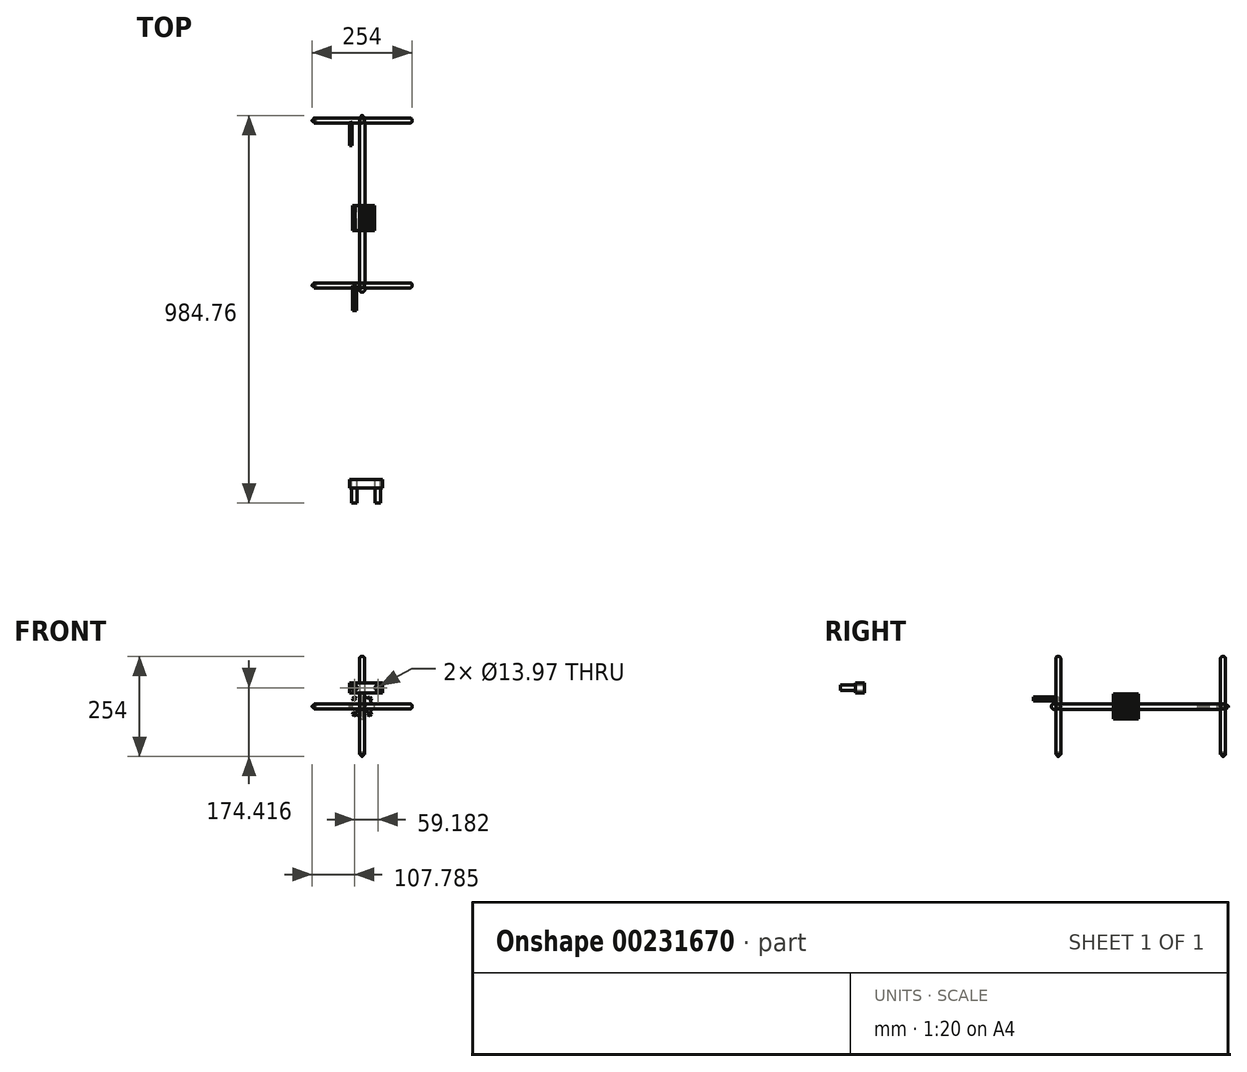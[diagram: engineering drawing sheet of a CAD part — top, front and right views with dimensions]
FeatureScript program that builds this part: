
annotation { "Feature Type Name" : "Feature", "Feature Type Description" : "" }
export const myFeature = defineFeature(function(context is Context, id is Id, definition is map)
    precondition{}
    {
        {
            var Q0;
            Q0=qCreatedBy(makeId("Front.planeOp"),FACE);
            var sketch = newSketch(context, id + "F0", { "sketchPlane" : qUnion([Q0])});
            skLineSegment(sketch, "E0", {"start": v(0, 0) * mm, "end": v(-17.96, 17.96) * mm});
            skArc(sketch, "E1", {"start": v(-17.96, 17.96) * mm, "mid": v(-9.72, 23.47) * mm, "end": v(0, 25.4) * mm});
            skLineSegment(sketch, "E2", {"start": v(0, 25.4) * mm, "end": v(0, 0) * mm});
            skLineSegment(sketch, "E3", {"start": v(-17.96, 17.96) * mm, "end": v(-22.45, 22.45) * mm});
            skLineSegment(sketch, "E4", {"start": v(-22.45, 22.45) * mm, "end": v(-20.65, 24.25) * mm});
            skLineSegment(sketch, "E5", {"start": v(-20.65, 24.25) * mm, "end": v(-14.3, 20.99) * mm});
            skLineSegment(sketch, "E6", {"start": v(0, 25.4) * mm, "end": v(0, 31.75) * mm});
            skLineSegment(sketch, "E7", {"start": v(0, 31.75) * mm, "end": v(-2.54, 31.75) * mm});
            skLineSegment(sketch, "E8", {"start": v(-2.54, 31.75) * mm, "end": v(-4.68, 24.97) * mm});
            skLineSegment(sketch, "E9.MirrorCS", {"start": v(0, 31.75) * mm, "end": v(2.54, 31.75) * mm});
            skLineSegment(sketch, "E10.MirrorCS", {"start": v(2.54, 31.75) * mm, "end": v(4.68, 24.97) * mm});
            skArc(sketch, "E11.MirrorCS", {"start": v(17.96, 17.96) * mm, "mid": v(9.72, 23.47) * mm, "end": v(0, 25.4) * mm});
            skLineSegment(sketch, "E12.MirrorCS", {"start": v(0, 0) * mm, "end": v(17.96, 17.96) * mm});
            skLineSegment(sketch, "E13.MirrorCS", {"start": v(20.65, 24.25) * mm, "end": v(14.3, 20.99) * mm});
            skLineSegment(sketch, "E14.MirrorCS", {"start": v(17.96, 17.96) * mm, "end": v(22.45, 22.45) * mm});
            skLineSegment(sketch, "E15.MirrorCS", {"start": v(22.45, 22.45) * mm, "end": v(20.65, 24.25) * mm});
            skLineSegment(sketch, "E16.MirrorCS", {"start": v(-22.45, -22.45) * mm, "end": v(-20.65, -24.25) * mm});
            skLineSegment(sketch, "E17.MirrorCS", {"start": v(0, -31.75) * mm, "end": v(2.54, -31.75) * mm});
            skLineSegment(sketch, "E18.MirrorCS", {"start": v(0, -31.75) * mm, "end": v(-2.54, -31.75) * mm});
            skLineSegment(sketch, "E19.MirrorCS", {"start": v(22.45, -22.45) * mm, "end": v(20.65, -24.25) * mm});
            skLineSegment(sketch, "E20.MirrorCS", {"start": v(-2.54, -31.75) * mm, "end": v(-4.68, -24.97) * mm});
            skLineSegment(sketch, "E21.MirrorCS", {"start": v(-20.65, -24.25) * mm, "end": v(-14.3, -20.99) * mm});
            skLineSegment(sketch, "E22.MirrorCS", {"start": v(-17.96, -17.96) * mm, "end": v(-22.45, -22.45) * mm});
            skLineSegment(sketch, "E23.MirrorCS", {"start": v(2.54, -31.75) * mm, "end": v(4.68, -24.97) * mm});
            skLineSegment(sketch, "E24.MirrorCS", {"start": v(20.65, -24.25) * mm, "end": v(14.3, -20.99) * mm});
            skArc(sketch, "E25.MirrorCS", {"start": v(17.96, -17.96) * mm, "mid": v(9.72, -23.47) * mm, "end": v(0, -25.4) * mm});
            skArc(sketch, "E26.MirrorCS", {"start": v(-17.96, -17.96) * mm, "mid": v(-9.72, -23.47) * mm, "end": v(0, -25.4) * mm});
            skLineSegment(sketch, "E27.MirrorCS", {"start": v(0, -25.4) * mm, "end": v(0, -31.75) * mm});
            skLineSegment(sketch, "E28.MirrorCS", {"start": v(17.96, -17.96) * mm, "end": v(22.45, -22.45) * mm});
            skLineSegment(sketch, "E29.MirrorCS", {"start": v(0, -25.4) * mm, "end": v(0, 0) * mm});
            skLineSegment(sketch, "E30.MirrorCS", {"start": v(0, 0) * mm, "end": v(17.96, -17.96) * mm});
            skLineSegment(sketch, "E31.MirrorCS", {"start": v(0, 0) * mm, "end": v(-17.96, -17.96) * mm});
            skLineSegment(sketch, "E32", {"start": v(-17.96, -17.96) * mm, "end": v(-29.23, -29.23) * mm, "construction": true});
            skLineSegment(sketch, "E33", {"start": v(-29.23, -29.23) * mm, "end": v(22.45, 22.45) * mm, "construction": true});
            skLineSegment(sketch, "E34.MirrorCS", {"start": v(24.25, -20.65) * mm, "end": v(20.99, -14.3) * mm});
            skLineSegment(sketch, "E35.MirrorCS", {"start": v(22.45, -22.45) * mm, "end": v(24.25, -20.65) * mm});
            skArc(sketch, "E36.MirrorCS", {"start": v(17.96, -17.96) * mm, "mid": v(23.47, -9.72) * mm, "end": v(25.4, 0) * mm});
            skArc(sketch, "E37.MirrorCS", {"start": v(17.96, 17.96) * mm, "mid": v(23.47, 9.72) * mm, "end": v(25.4, 0) * mm});
            skLineSegment(sketch, "E38.MirrorCS", {"start": v(24.25, 20.65) * mm, "end": v(20.99, 14.3) * mm});
            skLineSegment(sketch, "E39.MirrorCS", {"start": v(22.45, 22.45) * mm, "end": v(24.25, 20.65) * mm});
            skLineSegment(sketch, "E40.MirrorCS", {"start": v(25.4, 0) * mm, "end": v(31.75, 0) * mm});
            skLineSegment(sketch, "E41.MirrorCS", {"start": v(31.75, 0) * mm, "end": v(31.75, 2.54) * mm});
            skLineSegment(sketch, "E42.MirrorCS", {"start": v(31.75, 2.54) * mm, "end": v(24.97, 4.68) * mm});
            skLineSegment(sketch, "E43.MirrorCS", {"start": v(31.75, -2.54) * mm, "end": v(24.97, -4.68) * mm});
            skLineSegment(sketch, "E44.MirrorCS", {"start": v(31.75, 0) * mm, "end": v(31.75, -2.54) * mm});
            skLineSegment(sketch, "E45.MirrorCS", {"start": v(-24.25, -20.65) * mm, "end": v(-20.99, -14.3) * mm});
            skLineSegment(sketch, "E46.MirrorCS", {"start": v(-22.45, -22.45) * mm, "end": v(-24.25, -20.65) * mm});
            skArc(sketch, "E47.MirrorCS", {"start": v(-17.96, -17.96) * mm, "mid": v(-23.47, -9.72) * mm, "end": v(-25.4, 0) * mm});
            skArc(sketch, "E48.MirrorCS", {"start": v(-17.96, 17.96) * mm, "mid": v(-23.47, 9.72) * mm, "end": v(-25.4, 0) * mm});
            skLineSegment(sketch, "E49.MirrorCS", {"start": v(-31.75, 2.54) * mm, "end": v(-24.97, 4.68) * mm});
            skLineSegment(sketch, "E50.MirrorCS", {"start": v(-31.75, -2.54) * mm, "end": v(-24.97, -4.68) * mm});
            skLineSegment(sketch, "E51.MirrorCS", {"start": v(-24.25, 20.65) * mm, "end": v(-20.99, 14.3) * mm});
            skLineSegment(sketch, "E52.MirrorCS", {"start": v(-22.45, 22.45) * mm, "end": v(-24.25, 20.65) * mm});
            skLineSegment(sketch, "E53.MirrorCS", {"start": v(-31.75, 0) * mm, "end": v(-31.75, 2.54) * mm});
            skLineSegment(sketch, "E54.MirrorCS", {"start": v(-31.75, 0) * mm, "end": v(-31.75, -2.54) * mm});
            skCircle(sketch, "E55", {"center": v(0, 0) * mm, "radius": 6.99 * mm});
            skSolve(sketch);
        }
        {
            var Q0;
            {var subQ0=sQuery(id+"F0.wireOp",EDGE,"E6");Q0=makeQuery(id+"F0.imprint","IMPRINT",FACE,{"disambiguationData":[TD([[makeQuery(id+"F0.imprint","IMPRINT",EDGE,{"derivedFrom":subQ0}),-1.0]])]});}
            var Q1;
            {var subQ0=sQuery(id+"F0.wireOp",EDGE,"E6");Q1=makeQuery(id+"F0.imprint","IMPRINT",FACE,{"disambiguationData":[TD([[makeQuery(id+"F0.imprint","IMPRINT",EDGE,{"derivedFrom":subQ0}),1.0]])]});}
            var Q2;
            {var subQ1=sQuery(id+"F0.wireOp",EDGE,"E1");var subQ4=makeQuery(id+"F0.imprint","INTERSECT",VERTEX,{"derivedFrom":[subQ1,sQuery(id+"F0.wireOp",EDGE,"E5")]});Q2=makeQuery(id+"F0.imprint","IMPRINT",FACE,{"disambiguationData":[TD([[makeQuery(id+"F0.imprint","IMPRINT",EDGE,{"disambiguationData":[TD([[subQ4,-1.0]])],"derivedFrom":subQ1}),-1.0]])]});}
            var Q3;
            {var subQ0=sQuery(id+"F0.wireOp",EDGE,"E3");Q3=makeQuery(id+"F0.imprint","IMPRINT",FACE,{"disambiguationData":[TD([[makeQuery(id+"F0.imprint","IMPRINT",EDGE,{"derivedFrom":subQ0}),-1.0]])]});}
            var Q4;
            {var subQ0=sQuery(id+"F0.wireOp",EDGE,"E3");Q4=makeQuery(id+"F0.imprint","IMPRINT",FACE,{"disambiguationData":[TD([[makeQuery(id+"F0.imprint","IMPRINT",EDGE,{"derivedFrom":subQ0}),1.0]])]});}
            var Q5;
            {var subQ0=sQuery(id+"F0.wireOp",EDGE,"E47.MirrorCS");var subQ1=makeQuery(id+"F0.imprint","INTERSECT",VERTEX,{"derivedFrom":[sQuery(id+"F0.wireOp",EDGE,"E45.MirrorCS"),subQ0]});Q5=makeQuery(id+"F0.imprint","IMPRINT",FACE,{"disambiguationData":[TD([[makeQuery(id+"F0.imprint","IMPRINT",EDGE,{"disambiguationData":[TD([[subQ1,-1.0]])],"derivedFrom":subQ0}),-1.0]])]});}
            var Q6;
            {var subQ1=sQuery(id+"F0.wireOp",EDGE,"E26.MirrorCS");var subQ5=makeQuery(id+"F0.imprint","INTERSECT",VERTEX,{"derivedFrom":[sQuery(id+"F0.wireOp",EDGE,"E20.MirrorCS"),subQ1]});Q6=makeQuery(id+"F0.imprint","IMPRINT",FACE,{"disambiguationData":[TD([[makeQuery(id+"F0.imprint","IMPRINT",EDGE,{"disambiguationData":[TD([[subQ5,1.0]])],"derivedFrom":subQ1}),1.0]])]});}
            var Q7;
            {var subQ0=sQuery(id+"F0.wireOp",EDGE,"E25.MirrorCS");var subQ1=makeQuery(id+"F0.imprint","INTERSECT",VERTEX,{"derivedFrom":[sQuery(id+"F0.wireOp",EDGE,"E23.MirrorCS"),subQ0]});Q7=makeQuery(id+"F0.imprint","IMPRINT",FACE,{"disambiguationData":[TD([[makeQuery(id+"F0.imprint","IMPRINT",EDGE,{"disambiguationData":[TD([[subQ1,1.0]])],"derivedFrom":subQ0}),-1.0]])]});}
            var Q8;
            {var subQ0=sQuery(id+"F0.wireOp",EDGE,"E36.MirrorCS");var subQ3=makeQuery(id+"F0.imprint","INTERSECT",VERTEX,{"derivedFrom":[sQuery(id+"F0.wireOp",EDGE,"E34.MirrorCS"),subQ0]});Q8=makeQuery(id+"F0.imprint","IMPRINT",FACE,{"disambiguationData":[TD([[makeQuery(id+"F0.imprint","IMPRINT",EDGE,{"disambiguationData":[TD([[subQ3,-1.0]])],"derivedFrom":subQ0}),1.0]])]});}
            var Q9;
            {var subQ0=sQuery(id+"F0.wireOp",EDGE,"E11.MirrorCS");var subQ3=makeQuery(id+"F0.imprint","INTERSECT",VERTEX,{"derivedFrom":[sQuery(id+"F0.wireOp",EDGE,"E10.MirrorCS"),subQ0]});Q9=makeQuery(id+"F0.imprint","IMPRINT",FACE,{"disambiguationData":[TD([[makeQuery(id+"F0.imprint","IMPRINT",EDGE,{"disambiguationData":[TD([[subQ3,1.0]])],"derivedFrom":subQ0}),1.0]])]});}
            var Q10;
            {var subQ0=sQuery(id+"F0.wireOp",EDGE,"E14.MirrorCS");Q10=makeQuery(id+"F0.imprint","IMPRINT",FACE,{"disambiguationData":[TD([[makeQuery(id+"F0.imprint","IMPRINT",EDGE,{"derivedFrom":subQ0}),-1.0]])]});}
            var Q11;
            {var subQ2=sQuery(id+"F0.wireOp",EDGE,"E13.MirrorCS");Q11=makeQuery(id+"F0.imprint","IMPRINT",FACE,{"disambiguationData":[TD([[makeQuery(id+"F0.imprint","IMPRINT",EDGE,{"derivedFrom":subQ2}),1.0]])]});}
            var Q12;
            {var subQ0=sQuery(id+"F0.wireOp",EDGE,"E40.MirrorCS");Q12=makeQuery(id+"F0.imprint","IMPRINT",FACE,{"disambiguationData":[TD([[makeQuery(id+"F0.imprint","IMPRINT",EDGE,{"derivedFrom":subQ0}),1.0]])]});}
            var Q13;
            {var subQ0=sQuery(id+"F0.wireOp",EDGE,"E40.MirrorCS");Q13=makeQuery(id+"F0.imprint","IMPRINT",FACE,{"disambiguationData":[TD([[makeQuery(id+"F0.imprint","IMPRINT",EDGE,{"derivedFrom":subQ0}),-1.0]])]});}
            var Q14;
            {var subQ0=sQuery(id+"F0.wireOp",EDGE,"E34.MirrorCS");Q14=makeQuery(id+"F0.imprint","IMPRINT",FACE,{"disambiguationData":[TD([[makeQuery(id+"F0.imprint","IMPRINT",EDGE,{"derivedFrom":subQ0}),1.0]])]});}
            var Q15;
            Q15=makeQuery(id+"F0.imprint","IMPRINT",FACE,{"disambiguationData":[TD([[makeQuery(id+"F0.imprint","IMPRINT",EDGE,{"derivedFrom":sQuery(id+"F0.wireOp",EDGE,"E19.MirrorCS")}),-1.0]])]});
            var Q16;
            Q16=makeQuery(id+"F0.imprint","IMPRINT",FACE,{"disambiguationData":[TD([[makeQuery(id+"F0.imprint","IMPRINT",EDGE,{"derivedFrom":sQuery(id+"F0.wireOp",EDGE,"E17.MirrorCS")}),1.0]])]});
            var Q17;
            Q17=makeQuery(id+"F0.imprint","IMPRINT",FACE,{"disambiguationData":[TD([[makeQuery(id+"F0.imprint","IMPRINT",EDGE,{"derivedFrom":sQuery(id+"F0.wireOp",EDGE,"E18.MirrorCS")}),-1.0]])]});
            var Q18;
            Q18=makeQuery(id+"F0.imprint","IMPRINT",FACE,{"disambiguationData":[TD([[makeQuery(id+"F0.imprint","IMPRINT",EDGE,{"derivedFrom":sQuery(id+"F0.wireOp",EDGE,"E16.MirrorCS")}),1.0]])]});
            var Q19;
            {var subQ0=sQuery(id+"F0.wireOp",EDGE,"E22.MirrorCS");Q19=makeQuery(id+"F0.imprint","IMPRINT",FACE,{"disambiguationData":[TD([[makeQuery(id+"F0.imprint","IMPRINT",EDGE,{"derivedFrom":subQ0}),-1.0]])]});}
            var Q20;
            {var subQ1=sQuery(id+"F0.wireOp",EDGE,"E49.MirrorCS");Q20=makeQuery(id+"F0.imprint","IMPRINT",FACE,{"disambiguationData":[TD([[makeQuery(id+"F0.imprint","IMPRINT",EDGE,{"derivedFrom":subQ1}),-1.0]])]});}
            extrude(context, id + "F1", {"entities" : qUnion([Q0, Q1, Q2, Q3, Q4, Q5, Q6, Q7, Q8, Q9, Q10, Q11, Q12, Q13, Q14, Q15, Q16, Q17, Q18, Q19, Q20]), "depth" : 63.5 * mm});
        }
        {
            var Q0;
            Q0=qCreatedBy(makeId("Front.planeOp"),FACE);
            var sketch = newSketch(context, id + "F2", { "sketchPlane" : qUnion([Q0])});
            skLineSegment(sketch, "E56", {"start": v(-19.22, 47.42) * mm, "end": v(39.97, 47.42) * mm, "construction": true});
            skCircle(sketch, "E57", {"center": v(-19.22, 47.42) * mm, "radius": 6.99 * mm});
            skCircle(sketch, "E58", {"center": v(39.97, 47.42) * mm, "radius": 6.99 * mm});
            skLineSegment(sketch, "E59.bottom", {"start": v(52.67, 60.12) * mm, "end": v(-31.92, 60.12) * mm});
            skLineSegment(sketch, "E59.top", {"start": v(52.67, 34.72) * mm, "end": v(-31.92, 34.72) * mm});
            skLineSegment(sketch, "E59.left", {"start": v(52.67, 60.12) * mm, "end": v(52.67, 34.72) * mm});
            skLineSegment(sketch, "E59.right", {"start": v(-31.92, 60.12) * mm, "end": v(-31.92, 34.72) * mm});
            skPoint(sketch, "E59.middle", {"position": v(10.38, 47.42) * mm});
            skSolve(sketch);
        }
        {
            var Q0;
            Q0=makeQuery(id+"F2.imprint","IMPRINT",FACE,{"disambiguationData":[TD([[makeQuery(id+"F2.imprint","IMPRINT",EDGE,{"derivedFrom":sQuery(id+"F2.wireOp",EDGE,"E57")}),1.0]])]});
            var Q1;
            Q1=makeQuery(id+"F2.imprint","IMPRINT",FACE,{"disambiguationData":[TD([[makeQuery(id+"F2.imprint","IMPRINT",EDGE,{"derivedFrom":sQuery(id+"F2.wireOp",EDGE,"E58")}),1.0]])]});
            extrude(context, id + "F3", {"entities" : qUnion([Q0, Q1]), "depth" : 60.2 * mm});
        }
        {
            var Q0;
            Q0 = qSketchRegion(id + "F2", true);
            extrude(context, id + "F4", {"entities" : qUnion([Q0]), "depth" : 22.35 * mm});
        }
        {
            var Q0;
            {var subQ1=sQuery(id+"F0.wireOp",EDGE,"E29.MirrorCS");var subQ3=sQuery(id+"F0.wireOp",EDGE,"E55");var subQ4=makeQuery(id+"F0.imprint","INTERSECT",VERTEX,{"derivedFrom":[subQ1,subQ3]});Q0=makeQuery(id+"F0.imprint","IMPRINT",FACE,{"disambiguationData":[TD([[makeQuery(id+"F0.imprint","IMPRINT",EDGE,{"disambiguationData":[TD([[subQ4,-1.0]])],"derivedFrom":subQ3}),1.0]])]});}
            var Q1;
            {var subQ1=sQuery(id+"F0.wireOp",EDGE,"E29.MirrorCS");var subQ3=sQuery(id+"F0.wireOp",EDGE,"E55");var subQ4=makeQuery(id+"F0.imprint","INTERSECT",VERTEX,{"derivedFrom":[subQ1,subQ3]});Q1=makeQuery(id+"F0.imprint","IMPRINT",FACE,{"disambiguationData":[TD([[makeQuery(id+"F0.imprint","IMPRINT",EDGE,{"disambiguationData":[TD([[subQ4,1.0]])],"derivedFrom":subQ3}),1.0]])]});}
            var Q2;
            {var subQ1=sQuery(id+"F0.wireOp",EDGE,"E0");var subQ3=sQuery(id+"F0.wireOp",EDGE,"E55");var subQ4=makeQuery(id+"F0.imprint","INTERSECT",VERTEX,{"derivedFrom":[subQ1,subQ3]});Q2=makeQuery(id+"F0.imprint","IMPRINT",FACE,{"disambiguationData":[TD([[makeQuery(id+"F0.imprint","IMPRINT",EDGE,{"disambiguationData":[TD([[subQ4,-1.0]])],"derivedFrom":subQ3}),1.0]])]});}
            var Q3;
            {var subQ1=sQuery(id+"F0.wireOp",EDGE,"E0");var subQ3=sQuery(id+"F0.wireOp",EDGE,"E55");var subQ4=makeQuery(id+"F0.imprint","INTERSECT",VERTEX,{"derivedFrom":[subQ1,subQ3]});Q3=makeQuery(id+"F0.imprint","IMPRINT",FACE,{"disambiguationData":[TD([[makeQuery(id+"F0.imprint","IMPRINT",EDGE,{"disambiguationData":[TD([[subQ4,1.0]])],"derivedFrom":subQ3}),1.0]])]});}
            var Q4;
            {var subQ1=sQuery(id+"F0.wireOp",EDGE,"E2");var subQ3=sQuery(id+"F0.wireOp",EDGE,"E55");var subQ4=makeQuery(id+"F0.imprint","INTERSECT",VERTEX,{"derivedFrom":[subQ1,subQ3]});Q4=makeQuery(id+"F0.imprint","IMPRINT",FACE,{"disambiguationData":[TD([[makeQuery(id+"F0.imprint","IMPRINT",EDGE,{"disambiguationData":[TD([[subQ4,1.0]])],"derivedFrom":subQ3}),1.0]])]});}
            var Q5;
            {var subQ1=sQuery(id+"F0.wireOp",EDGE,"E12.MirrorCS");var subQ3=sQuery(id+"F0.wireOp",EDGE,"E55");var subQ4=makeQuery(id+"F0.imprint","INTERSECT",VERTEX,{"derivedFrom":[subQ1,subQ3]});Q5=makeQuery(id+"F0.imprint","IMPRINT",FACE,{"disambiguationData":[TD([[makeQuery(id+"F0.imprint","IMPRINT",EDGE,{"disambiguationData":[TD([[subQ4,1.0]])],"derivedFrom":subQ3}),1.0]])]});}
            extrude(context, id + "F5", {"entities" : qUnion([Q0, Q1, Q2, Q3, Q4, Q5]), "operationType" : NewBodyOperationType.ADD, "oppositeDirection" : true, "depth" : 228.6 * mm, "hasSecondDirection" : true, "secondDirectionOppositeDirection" : false, "secondDirectionDepth" : 219.96 * mm});
        }
        {
            var Q0;
            Q0=makeQuery(id+"F1.opExtrude","SWEPT_BODY",BODY,{"disambiguationData":[OSD([sQuery(id+"F0.wireOp",EDGE,"E1"),sQuery(id+"F0.wireOp",EDGE,"E4"),sQuery(id+"F0.wireOp",EDGE,"E5"),sQuery(id+"F0.wireOp",EDGE,"E7"),sQuery(id+"F0.wireOp",EDGE,"E8"),sQuery(id+"F0.wireOp",EDGE,"E9.MirrorCS"),sQuery(id+"F0.wireOp",EDGE,"E10.MirrorCS"),sQuery(id+"F0.wireOp",EDGE,"E11.MirrorCS"),sQuery(id+"F0.wireOp",EDGE,"E13.MirrorCS"),sQuery(id+"F0.wireOp",EDGE,"E15.MirrorCS"),sQuery(id+"F0.wireOp",EDGE,"E16.MirrorCS"),sQuery(id+"F0.wireOp",EDGE,"E17.MirrorCS"),sQuery(id+"F0.wireOp",EDGE,"E18.MirrorCS"),sQuery(id+"F0.wireOp",EDGE,"E19.MirrorCS"),sQuery(id+"F0.wireOp",EDGE,"E20.MirrorCS"),sQuery(id+"F0.wireOp",EDGE,"E21.MirrorCS"),sQuery(id+"F0.wireOp",EDGE,"E23.MirrorCS"),sQuery(id+"F0.wireOp",EDGE,"E24.MirrorCS"),sQuery(id+"F0.wireOp",EDGE,"E25.MirrorCS"),sQuery(id+"F0.wireOp",EDGE,"E26.MirrorCS"),sQuery(id+"F0.wireOp",EDGE,"E34.MirrorCS"),sQuery(id+"F0.wireOp",EDGE,"E35.MirrorCS"),sQuery(id+"F0.wireOp",EDGE,"E36.MirrorCS"),sQuery(id+"F0.wireOp",EDGE,"E37.MirrorCS"),sQuery(id+"F0.wireOp",EDGE,"E38.MirrorCS"),sQuery(id+"F0.wireOp",EDGE,"E39.MirrorCS"),sQuery(id+"F0.wireOp",EDGE,"E41.MirrorCS"),sQuery(id+"F0.wireOp",EDGE,"E42.MirrorCS"),sQuery(id+"F0.wireOp",EDGE,"E43.MirrorCS"),sQuery(id+"F0.wireOp",EDGE,"E44.MirrorCS"),sQuery(id+"F0.wireOp",EDGE,"E45.MirrorCS"),sQuery(id+"F0.wireOp",EDGE,"E46.MirrorCS"),sQuery(id+"F0.wireOp",EDGE,"E47.MirrorCS"),sQuery(id+"F0.wireOp",EDGE,"E48.MirrorCS"),sQuery(id+"F0.wireOp",EDGE,"E49.MirrorCS"),sQuery(id+"F0.wireOp",EDGE,"E50.MirrorCS"),sQuery(id+"F0.wireOp",EDGE,"E51.MirrorCS"),sQuery(id+"F0.wireOp",EDGE,"E52.MirrorCS"),sQuery(id+"F0.wireOp",EDGE,"E53.MirrorCS"),sQuery(id+"F0.wireOp",EDGE,"E54.MirrorCS"),sQuery(id+"F0.wireOp",EDGE,"E55")])]});
            transform(context, id + "F6", {"entities" : qUnion([Q0]), "transformType" : TransformType.TRANSLATION_3D, "dx" : 0 * mm, "dy" : -132.08 * mm, "dz" : 0 * mm, "makeCopy" : false});
        }
        {
            var Q0;
            Q0=makeQuery(id+"F5.opExtrude","CAP_EDGE",EDGE,{"disambiguationData":[OSD([sQuery(id+"F0.wireOp",EDGE,"E55")])],"isStart":false});
            var Q1;
            Q1=makeQuery(id+"FoJtG7K4DBaO0Y3_4.opExtrude","CAP_EDGE",EDGE,{"disambiguationData":[OSD([sQuery(id+"FWvqbfKtp3cxLVg_4.wireOp",EDGE,"aRqvi6iJ-hhy7-xzrE-r3em-tmQ5B9AIq148")])],"isStart":true});
            var Q2;
            Q2=makeQuery(id+"FoJtG7K4DBaO0Y3_4.opExtrude","CAP_EDGE",EDGE,{"disambiguationData":[OSD([sQuery(id+"FWvqbfKtp3cxLVg_4.wireOp",EDGE,"aRqvi6iJ-hhy7-xzrE-r3em-tmQ5B9AIq148")])],"isStart":false});
            fillet(context, id + "F7", {"entities" : qUnion([Q0, Q1, Q2]), "radius" : 5.08 * mm, "tangentPropagation" : true, "allowEdgeOverflow" : false});
        }
        {
            var Q0;
            Q0=makeQuery(id+"F1.opExtrude","SWEPT_BODY",BODY,{"disambiguationData":[OSD([sQuery(id+"F0.wireOp",EDGE,"E1"),sQuery(id+"F0.wireOp",EDGE,"E4"),sQuery(id+"F0.wireOp",EDGE,"E5"),sQuery(id+"F0.wireOp",EDGE,"E7"),sQuery(id+"F0.wireOp",EDGE,"E8"),sQuery(id+"F0.wireOp",EDGE,"E9.MirrorCS"),sQuery(id+"F0.wireOp",EDGE,"E10.MirrorCS"),sQuery(id+"F0.wireOp",EDGE,"E11.MirrorCS"),sQuery(id+"F0.wireOp",EDGE,"E13.MirrorCS"),sQuery(id+"F0.wireOp",EDGE,"E15.MirrorCS"),sQuery(id+"F0.wireOp",EDGE,"E16.MirrorCS"),sQuery(id+"F0.wireOp",EDGE,"E17.MirrorCS"),sQuery(id+"F0.wireOp",EDGE,"E18.MirrorCS"),sQuery(id+"F0.wireOp",EDGE,"E19.MirrorCS"),sQuery(id+"F0.wireOp",EDGE,"E20.MirrorCS"),sQuery(id+"F0.wireOp",EDGE,"E21.MirrorCS"),sQuery(id+"F0.wireOp",EDGE,"E23.MirrorCS"),sQuery(id+"F0.wireOp",EDGE,"E24.MirrorCS"),sQuery(id+"F0.wireOp",EDGE,"E25.MirrorCS"),sQuery(id+"F0.wireOp",EDGE,"E26.MirrorCS"),sQuery(id+"F0.wireOp",EDGE,"E34.MirrorCS"),sQuery(id+"F0.wireOp",EDGE,"E35.MirrorCS"),sQuery(id+"F0.wireOp",EDGE,"E36.MirrorCS"),sQuery(id+"F0.wireOp",EDGE,"E37.MirrorCS"),sQuery(id+"F0.wireOp",EDGE,"E38.MirrorCS"),sQuery(id+"F0.wireOp",EDGE,"E39.MirrorCS"),sQuery(id+"F0.wireOp",EDGE,"E41.MirrorCS"),sQuery(id+"F0.wireOp",EDGE,"E42.MirrorCS"),sQuery(id+"F0.wireOp",EDGE,"E43.MirrorCS"),sQuery(id+"F0.wireOp",EDGE,"E44.MirrorCS"),sQuery(id+"F0.wireOp",EDGE,"E45.MirrorCS"),sQuery(id+"F0.wireOp",EDGE,"E46.MirrorCS"),sQuery(id+"F0.wireOp",EDGE,"E47.MirrorCS"),sQuery(id+"F0.wireOp",EDGE,"E48.MirrorCS"),sQuery(id+"F0.wireOp",EDGE,"E49.MirrorCS"),sQuery(id+"F0.wireOp",EDGE,"E50.MirrorCS"),sQuery(id+"F0.wireOp",EDGE,"E51.MirrorCS"),sQuery(id+"F0.wireOp",EDGE,"E52.MirrorCS"),sQuery(id+"F0.wireOp",EDGE,"E53.MirrorCS"),sQuery(id+"F0.wireOp",EDGE,"E54.MirrorCS"),sQuery(id+"F0.wireOp",EDGE,"E55")])]});
            transform(context, id + "F8", {"entities" : qUnion([Q0]), "transformType" : TransformType.TRANSLATION_3D, "dx" : 0 * mm, "dy" : -83.57 * mm, "dz" : 0 * mm, "makeCopy" : false});
        }
        {
            var Q0;
            Q0=qCreatedBy(makeId("Right.planeOp"),FACE);
            var sketch = newSketch(context, id + "F9", { "sketchPlane" : qUnion([Q0])});
            skCircle(sketch, "E60", {"center": v(0, 0) * mm, "radius": 6.35 * mm});
            skSolve(sketch);
        }
        {
            var Q0;
            Q0 = qSketchRegion(id + "F9", true);
            extrude(context, id + "F10", {"entities" : qUnion([Q0]), "operationType" : NewBodyOperationType.ADD, "depth" : 127 * mm, "hasSecondDirection" : true, "secondDirectionOppositeDirection" : true, "secondDirectionDepth" : 127 * mm});
        }
        {
            var Q0;
            Q0=makeQuery(id+"F10.opExtrude","CAP_EDGE",EDGE,{"disambiguationData":[OSD([sQuery(id+"F9.wireOp",EDGE,"E60")])],"isStart":true});
            var Q1;
            Q1=makeQuery(id+"F10.opExtrude","CAP_EDGE",EDGE,{"disambiguationData":[OSD([sQuery(id+"F9.wireOp",EDGE,"E60")])],"isStart":false});
            fillet(context, id + "F11", {"entities" : qUnion([Q0, Q1]), "radius" : 5.08 * mm, "tangentPropagation" : true, "allowEdgeOverflow" : false});
        }
        {
            var Q0;
            Q0=makeQuery(id+"F3.opExtrude","SWEPT_BODY",BODY,{"disambiguationData":[OSD([sQuery(id+"F2.wireOp",EDGE,"E57")])]});
            var Q1;
            Q1=makeQuery(id+"F4.opExtrude","SWEPT_BODY",BODY,{"disambiguationData":[OSD([sQuery(id+"F2.wireOp",EDGE,"E57"),sQuery(id+"F2.wireOp",EDGE,"E58"),sQuery(id+"F2.wireOp",EDGE,"E59.bottom"),sQuery(id+"F2.wireOp",EDGE,"E59.top"),sQuery(id+"F2.wireOp",EDGE,"E59.left"),sQuery(id+"F2.wireOp",EDGE,"E59.right")])]});
            var Q2;
            Q2=makeQuery(id+"F3.opExtrude","SWEPT_BODY",BODY,{"disambiguationData":[OSD([sQuery(id+"F2.wireOp",EDGE,"E58")])]});
            transform(context, id + "F12", {"entities" : qUnion([Q0, Q1, Q2]), "transformType" : TransformType.TRANSLATION_3D, "dx" : 0 * mm, "dy" : -492.76 * mm, "dz" : 0 * mm, "makeCopy" : false});
        }
        {
            var Q0;
            Q0=qCreatedBy(makeId("Top.planeOp"),FACE);
            var sketch = newSketch(context, id + "F13", { "sketchPlane" : qUnion([Q0])});
            skCircle(sketch, "E61", {"center": v(0, 0) * mm, "radius": 6.35 * mm});
            skSolve(sketch);
        }
        {
            var Q0;
            Q0 = qSketchRegion(id + "F13", true);
            extrude(context, id + "F14", {"entities" : qUnion([Q0]), "operationType" : NewBodyOperationType.ADD, "depth" : 127 * mm, "hasSecondDirection" : true, "secondDirectionOppositeDirection" : true, "secondDirectionDepth" : 127 * mm});
        }
        {
            var Q0;
            Q0=makeQuery(id+"F14.opExtrude","CAP_EDGE",EDGE,{"disambiguationData":[OSD([sQuery(id+"F13.wireOp",EDGE,"E61")])],"isStart":false});
            var Q1;
            Q1=makeQuery(id+"F14.opExtrude","CAP_EDGE",EDGE,{"disambiguationData":[OSD([sQuery(id+"F13.wireOp",EDGE,"E61")])],"isStart":true});
            fillet(context, id + "F15", {"entities" : qUnion([Q0, Q1]), "radius" : 5.08 * mm, "tangentPropagation" : true, "allowEdgeOverflow" : false});
        }
        {
            var Q0;
            Q0=makeQuery(id+"F5.opExtrude","CAP_EDGE",EDGE,{"disambiguationData":[OSD([sQuery(id+"F0.wireOp",EDGE,"E55")])],"isStart":true});
            fillet(context, id + "F16", {"entities" : qUnion([Q0]), "radius" : 5.08 * mm, "tangentPropagation" : true, "allowEdgeOverflow" : false});
        }
        {
            var Q0;
            Q0=makeQuery(id+"F1.opExtrude","SWEPT_BODY",BODY,{"disambiguationData":[OSD([sQuery(id+"F0.wireOp",EDGE,"E1"),sQuery(id+"F0.wireOp",EDGE,"E4"),sQuery(id+"F0.wireOp",EDGE,"E5"),sQuery(id+"F0.wireOp",EDGE,"E7"),sQuery(id+"F0.wireOp",EDGE,"E8"),sQuery(id+"F0.wireOp",EDGE,"E9.MirrorCS"),sQuery(id+"F0.wireOp",EDGE,"E10.MirrorCS"),sQuery(id+"F0.wireOp",EDGE,"E11.MirrorCS"),sQuery(id+"F0.wireOp",EDGE,"E13.MirrorCS"),sQuery(id+"F0.wireOp",EDGE,"E15.MirrorCS"),sQuery(id+"F0.wireOp",EDGE,"E16.MirrorCS"),sQuery(id+"F0.wireOp",EDGE,"E17.MirrorCS"),sQuery(id+"F0.wireOp",EDGE,"E18.MirrorCS"),sQuery(id+"F0.wireOp",EDGE,"E19.MirrorCS"),sQuery(id+"F0.wireOp",EDGE,"E20.MirrorCS"),sQuery(id+"F0.wireOp",EDGE,"E21.MirrorCS"),sQuery(id+"F0.wireOp",EDGE,"E23.MirrorCS"),sQuery(id+"F0.wireOp",EDGE,"E24.MirrorCS"),sQuery(id+"F0.wireOp",EDGE,"E25.MirrorCS"),sQuery(id+"F0.wireOp",EDGE,"E26.MirrorCS"),sQuery(id+"F0.wireOp",EDGE,"E34.MirrorCS"),sQuery(id+"F0.wireOp",EDGE,"E35.MirrorCS"),sQuery(id+"F0.wireOp",EDGE,"E36.MirrorCS"),sQuery(id+"F0.wireOp",EDGE,"E37.MirrorCS"),sQuery(id+"F0.wireOp",EDGE,"E38.MirrorCS"),sQuery(id+"F0.wireOp",EDGE,"E39.MirrorCS"),sQuery(id+"F0.wireOp",EDGE,"E41.MirrorCS"),sQuery(id+"F0.wireOp",EDGE,"E42.MirrorCS"),sQuery(id+"F0.wireOp",EDGE,"E43.MirrorCS"),sQuery(id+"F0.wireOp",EDGE,"E44.MirrorCS"),sQuery(id+"F0.wireOp",EDGE,"E45.MirrorCS"),sQuery(id+"F0.wireOp",EDGE,"E46.MirrorCS"),sQuery(id+"F0.wireOp",EDGE,"E47.MirrorCS"),sQuery(id+"F0.wireOp",EDGE,"E48.MirrorCS"),sQuery(id+"F0.wireOp",EDGE,"E49.MirrorCS"),sQuery(id+"F0.wireOp",EDGE,"E50.MirrorCS"),sQuery(id+"F0.wireOp",EDGE,"E51.MirrorCS"),sQuery(id+"F0.wireOp",EDGE,"E52.MirrorCS"),sQuery(id+"F0.wireOp",EDGE,"E53.MirrorCS"),sQuery(id+"F0.wireOp",EDGE,"E54.MirrorCS"),sQuery(id+"F0.wireOp",EDGE,"E55")])]});
            transform(context, id + "F17", {"entities" : qUnion([Q0]), "transformType" : TransformType.TRANSLATION_3D, "dx" : 0 * mm, "dy" : 418.85 * mm, "dz" : 0 * mm, "makeCopy" : false});
        }
        {
            var Q0;
            Q0=qCreatedBy(makeId("Top.planeOp"),FACE);
            var sketch = newSketch(context, id + "F18", { "sketchPlane" : qUnion([Q0])});
            skCircle(sketch, "E62", {"center": v(0, 0) * mm, "radius": 6.35 * mm});
            skSolve(sketch);
        }
        {
            var Q0;
            Q0 = qSketchRegion(id + "F18", true);
            extrude(context, id + "F19", {"entities" : qUnion([Q0]), "operationType" : NewBodyOperationType.ADD, "depth" : 127 * mm, "hasSecondDirection" : true, "secondDirectionOppositeDirection" : true, "secondDirectionDepth" : 127 * mm});
        }
        {
            var Q0;
            Q0=qCreatedBy(makeId("Right.planeOp"),FACE);
            var sketch = newSketch(context, id + "F20", { "sketchPlane" : qUnion([Q0])});
            skCircle(sketch, "E63", {"center": v(0, 0) * mm, "radius": 6.35 * mm});
            skSolve(sketch);
        }
        {
            var Q0;
            Q0 = qSketchRegion(id + "F20", true);
            extrude(context, id + "F21", {"entities" : qUnion([Q0]), "operationType" : NewBodyOperationType.ADD, "depth" : 127 * mm, "hasSecondDirection" : true, "secondDirectionOppositeDirection" : true, "secondDirectionDepth" : 127 * mm});
        }
        {
            var Q0;
            Q0=makeQuery(id+"F21.opExtrude","CAP_EDGE",EDGE,{"disambiguationData":[OSD([sQuery(id+"F20.wireOp",EDGE,"E63")])],"isStart":false});
            var Q1;
            Q1=makeQuery(id+"F19.opExtrude","CAP_EDGE",EDGE,{"disambiguationData":[OSD([sQuery(id+"F18.wireOp",EDGE,"E62")])],"isStart":true});
            var Q2;
            Q2=makeQuery(id+"F21.opExtrude","CAP_EDGE",EDGE,{"disambiguationData":[OSD([sQuery(id+"F20.wireOp",EDGE,"E63")])],"isStart":true});
            var Q3;
            Q3=makeQuery(id+"F19.opExtrude","CAP_EDGE",EDGE,{"disambiguationData":[OSD([sQuery(id+"F18.wireOp",EDGE,"E62")])],"isStart":false});
            fillet(context, id + "F22", {"entities" : qUnion([Q0, Q1, Q2, Q3]), "radius" : 5.08 * mm, "tangentPropagation" : true, "allowEdgeOverflow" : false});
        }
    });
